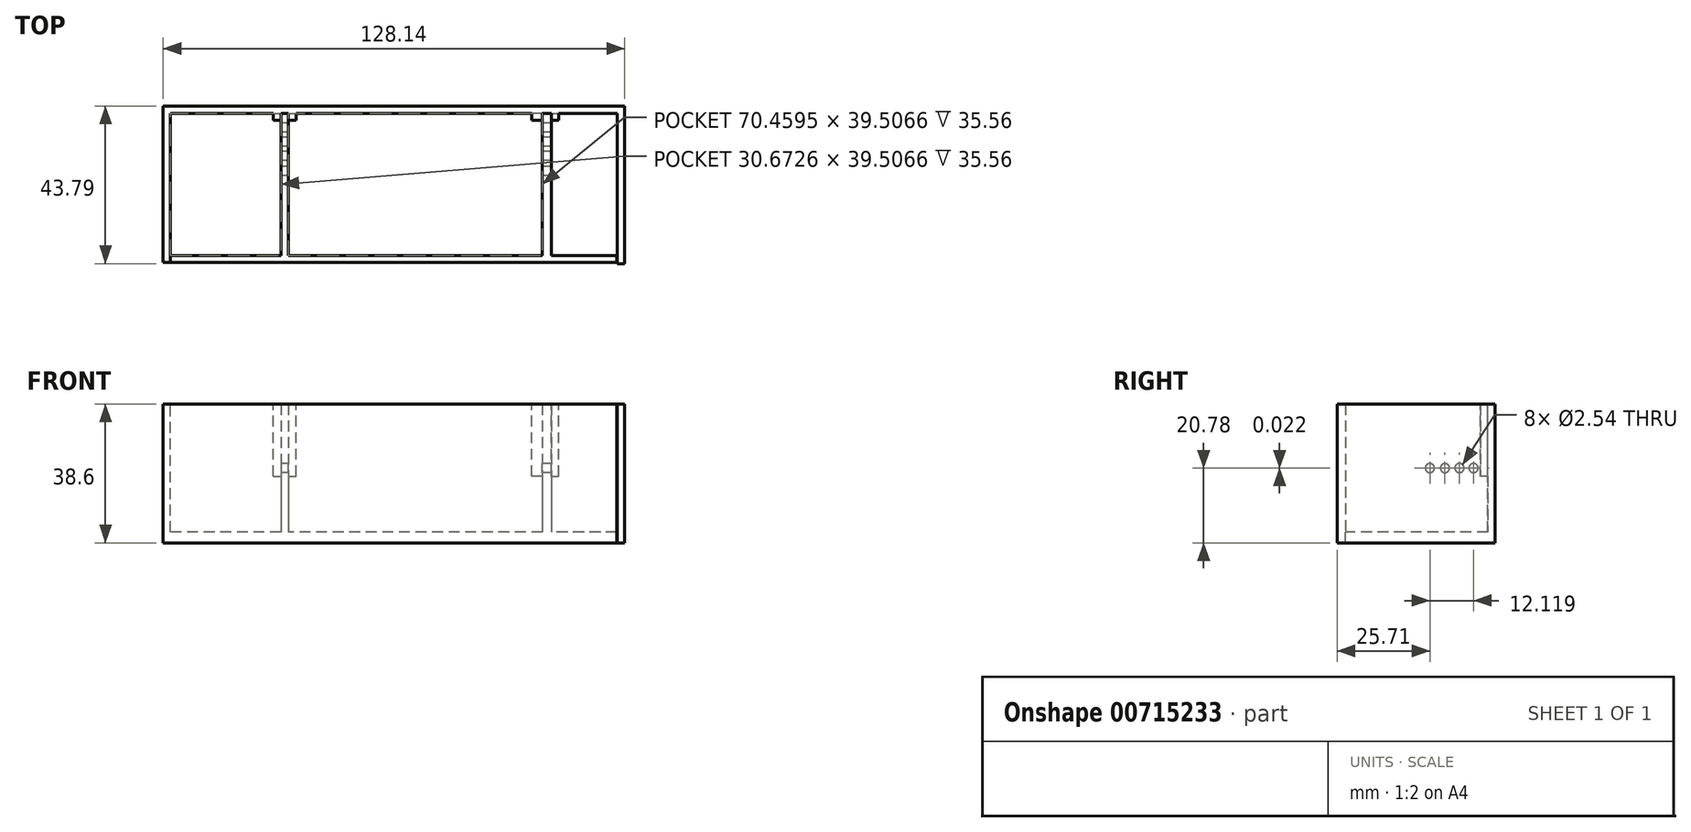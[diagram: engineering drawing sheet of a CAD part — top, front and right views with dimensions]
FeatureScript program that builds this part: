
annotation { "Feature Type Name" : "Feature", "Feature Type Description" : "" }
export const myFeature = defineFeature(function(context is Context, id is Id, definition is map)
    precondition{}
    {
        {
            var Q0;
            Q0=qCreatedBy(makeId("Top.planeOp"),FACE);
            var sketch = newSketch(context, id + "F0", { "sketchPlane" : qUnion([Q0])});
            skLineSegment(sketch, "E0.bottom", {"start": v(62.07, 19.75) * mm, "end": v(-62.07, 19.75) * mm});
            skLineSegment(sketch, "E0.top", {"start": v(62.07, -19.75) * mm, "end": v(-62.07, -19.75) * mm});
            skLineSegment(sketch, "E0.left", {"start": v(62.07, 19.75) * mm, "end": v(62.07, -19.75) * mm});
            skLineSegment(sketch, "E0.right", {"start": v(-62.07, 19.75) * mm, "end": v(-62.07, -19.75) * mm});
            skPoint(sketch, "E0.middle", {"position": v(0, 0) * mm});
            skSolve(sketch);
        }
        {
            var Q0;
            Q0=makeQuery(id+"F0.imprint","IMPRINT",FACE,{"disambiguationData":[TD([[makeQuery(id+"F0.imprint","IMPRINT",EDGE,{"derivedFrom":sQuery(id+"F0.wireOp",EDGE,"E0.bottom")}),1.0]])]});
            extrude(context, id + "F1", {"entities" : qUnion([Q0]), "depth" : 3 * mm, "offsetDistance" : 25.4 * mm});
        }
        {
            var Q0;
            Q0=makeQuery(id+"F1.opExtrude","CAP_FACE",FACE,{"disambiguationData":[OSD([sQuery(id+"F0.wireOp",EDGE,"E0.bottom"),sQuery(id+"F0.wireOp",EDGE,"E0.top"),sQuery(id+"F0.wireOp",EDGE,"E0.left"),sQuery(id+"F0.wireOp",EDGE,"E0.right")])],"isStart":false});
            var sketch = newSketch(context, id + "F2", { "sketchPlane" : qUnion([Q0])});
            skLineSegment(sketch, "E1.bottom", {"start": v(43.71, 19.75) * mm, "end": v(41.21, 19.75) * mm});
            skLineSegment(sketch, "E1.top", {"start": v(43.71, -19.75) * mm, "end": v(41.21, -19.75) * mm});
            skLineSegment(sketch, "E1.left", {"start": v(43.71, 19.75) * mm, "end": v(43.71, -19.75) * mm});
            skLineSegment(sketch, "E1.right", {"start": v(41.21, 19.75) * mm, "end": v(41.21, -19.75) * mm});
            skLineSegment(sketch, "E2.bottom", {"start": v(-29.25, 19.75) * mm, "end": v(-31.4, 19.75) * mm});
            skLineSegment(sketch, "E2.top", {"start": v(-29.25, -19.75) * mm, "end": v(-31.4, -19.75) * mm});
            skLineSegment(sketch, "E2.left", {"start": v(-29.25, 19.75) * mm, "end": v(-29.25, -19.75) * mm});
            skLineSegment(sketch, "E2.right", {"start": v(-31.4, 19.75) * mm, "end": v(-31.4, -19.75) * mm});
            skSolve(sketch);
        }
        {
            var Q0;
            Q0=makeQuery(id+"F2.imprint","IMPRINT",FACE,{"disambiguationData":[TD([[makeQuery(id+"F2.imprint","IMPRINT",EDGE,{"derivedFrom":sQuery(id+"F2.wireOp",EDGE,"E1.bottom")}),1.0]])]});
            var Q1;
            Q1=makeQuery(id+"F2.imprint","IMPRINT",FACE,{"disambiguationData":[TD([[makeQuery(id+"F2.imprint","IMPRINT",EDGE,{"derivedFrom":sQuery(id+"F2.wireOp",EDGE,"E2.bottom")}),1.0]])]});
            extrude(context, id + "F3", {"entities" : qUnion([Q0, Q1]), "operationType" : NewBodyOperationType.ADD, "depth" : 17.78 * mm, "offsetDistance" : 25.4 * mm});
        }
        {
            var Q0;
            Q0=makeQuery(id+"F3.opExtrude","SWEPT_FACE",FACE,{"disambiguationData":[OSD([sQuery(id+"F2.wireOp",EDGE,"E2.right")])]});
            var sketch = newSketch(context, id + "F4", { "sketchPlane" : qUnion([Q0])});
            skSolve(sketch);
        }
        {
            var Q0;
            Q0=makeQuery(id+"F3.opExtrude","CAP_FACE",FACE,{"disambiguationData":[OSD([sQuery(id+"F2.wireOp",EDGE,"E2.bottom"),sQuery(id+"F2.wireOp",EDGE,"E2.top"),sQuery(id+"F2.wireOp",EDGE,"E2.left"),sQuery(id+"F2.wireOp",EDGE,"E2.right")])],"isStart":false});
            var Q1;
            Q1=makeQuery(id+"F3.opExtrude","CAP_FACE",FACE,{"disambiguationData":[OSD([sQuery(id+"F2.wireOp",EDGE,"E1.bottom"),sQuery(id+"F2.wireOp",EDGE,"E1.top"),sQuery(id+"F2.wireOp",EDGE,"E1.left"),sQuery(id+"F2.wireOp",EDGE,"E1.right")])],"isStart":false});
            extrude(context, id + "F5", {"entities" : qUnion([Q0, Q1]), "operationType" : NewBodyOperationType.ADD, "depth" : 17.78 * mm, "offsetDistance" : 25.4 * mm});
        }
        {
            var Q0;
            {var subQ0=sQuery(id+"F2.wireOp",EDGE,"E2.right");Q0=makeQuery(id+"F5.boolean.opBoolean","MERGE",FACE,{"derivedFrom":[makeQuery(id+"F3.opExtrude","SWEPT_FACE",FACE,{"disambiguationData":[OSD([subQ0])]}),makeQuery(id+"F5.opExtrude","SWEPT_FACE",FACE,{"disambiguationData":[OSD([subQ0])]})]});}
            var sketch = newSketch(context, id + "F6", { "sketchPlane" : qUnion([Q0])});
            skCircle(sketch, "E3", {"center": v(-15.79, 20.8) * mm, "radius": 1.27 * mm});
            skCircle(sketch, "E4", {"center": v(-11.89, 20.8) * mm, "radius": 1.27 * mm});
            skCircle(sketch, "E5", {"center": v(-7.85, 20.78) * mm, "radius": 1.27 * mm});
            skCircle(sketch, "E6", {"center": v(-3.67, 20.79) * mm, "radius": 1.27 * mm});
            skSolve(sketch);
        }
        {
            var Q0;
            Q0=sQuery(id+"F6.wireOp",VERTEX,"E4.center");
            var Q1;
            Q1=sQuery(id+"F6.wireOp",VERTEX,"E3.center");
            var Q2;
            Q2=sQuery(id+"F6.wireOp",VERTEX,"E5.center");
            var Q3;
            Q3=sQuery(id+"F6.wireOp",VERTEX,"E6.center");
            var Q4;
            Q4=makeQuery(id+"F1.opExtrude","SWEPT_BODY",BODY,{"disambiguationData":[OSD([sQuery(id+"F0.wireOp",EDGE,"E0.bottom"),sQuery(id+"F0.wireOp",EDGE,"E0.top"),sQuery(id+"F0.wireOp",EDGE,"E0.left"),sQuery(id+"F0.wireOp",EDGE,"E0.right")])]});
            hole(context, id + "F7", {"style" : HoleStyle.SIMPLE, "endStyle" : HoleEndStyle.THROUGH, "holeDiameter" : 2.54 * mm, "majorDiameter" : 6.35 * mm, "isTappedThrough" : true, "tappedDepth" : 12.7 * mm, "tapClearance" : 3, "locations" : qUnion([Q0, Q1, Q2, Q3]), "scope" : qUnion([Q4])});
        }
        {
            var Q0;
            {var subQ0=sQuery(id+"F2.wireOp",EDGE,"E2.top");var subQ1=sQuery(id+"F2.wireOp",EDGE,"E1.top");Q0=makeQuery(id+"F5.boolean.opBoolean","MERGE",FACE,{"derivedFrom":[makeQuery(id+"F3.boolean.opBoolean","MERGE",FACE,{"derivedFrom":[makeQuery(id+"F1.opExtrude","SWEPT_FACE",FACE,{"disambiguationData":[OSD([sQuery(id+"F0.wireOp",EDGE,"E0.top")])]}),makeQuery(id+"F3.opExtrude","SWEPT_FACE",FACE,{"disambiguationData":[OSD([subQ1])]}),makeQuery(id+"F3.opExtrude","SWEPT_FACE",FACE,{"disambiguationData":[OSD([subQ0])]})]}),makeQuery(id+"F5.opExtrude","SWEPT_FACE",FACE,{"disambiguationData":[OSD([subQ1])]}),makeQuery(id+"F5.opExtrude","SWEPT_FACE",FACE,{"disambiguationData":[OSD([subQ0])]})]});}
            var sketch = newSketch(context, id + "F8", { "sketchPlane" : qUnion([Q0])});
            skLineSegment(sketch, "E7.bottom", {"start": v(-62.07, 0) * mm, "end": v(61.89, 0) * mm});
            skLineSegment(sketch, "E7.top", {"start": v(-62.07, 38.56) * mm, "end": v(61.89, 38.56) * mm});
            skLineSegment(sketch, "E7.left", {"start": v(-62.07, 0) * mm, "end": v(-62.07, 38.56) * mm});
            skLineSegment(sketch, "E7.right", {"start": v(61.89, 0) * mm, "end": v(61.89, 38.56) * mm});
            skSolve(sketch);
        }
        {
            var Q0;
            {var subQ1=sQuery(id+"F2.wireOp",EDGE,"E2.right");var subQ2=sQuery(id+"F2.wireOp",EDGE,"E2.top");var subQ3=sQuery(id+"F0.wireOp",EDGE,"E0.top");var subQ4=makeQuery(id+"F5.boolean.opBoolean","MERGE",EDGE,{"derivedFrom":[makeQuery(id+"F3.opExtrude","SWEPT_EDGE",EDGE,{"disambiguationData":[OSD([subQ3,subQ2,subQ1])]}),makeQuery(id+"F5.opExtrude","SWEPT_EDGE",EDGE,{"disambiguationData":[OSD([subQ3,subQ2,subQ1])]})]});Q0=makeQuery(id+"F8.imprint","IMPRINT",FACE,{"disambiguationData":[TD([[makeQuery(id+"F8.imprint","IMPRINT",EDGE,{"derivedFrom":subQ4}),-1.0]])]});}
            var Q1;
            {var subQ1=sQuery(id+"F2.wireOp",EDGE,"E1.right");var subQ2=sQuery(id+"F2.wireOp",EDGE,"E1.top");var subQ3=sQuery(id+"F0.wireOp",EDGE,"E0.top");var subQ4=makeQuery(id+"F5.boolean.opBoolean","MERGE",EDGE,{"derivedFrom":[makeQuery(id+"F3.opExtrude","SWEPT_EDGE",EDGE,{"disambiguationData":[OSD([subQ3,subQ2,subQ1])]}),makeQuery(id+"F5.opExtrude","SWEPT_EDGE",EDGE,{"disambiguationData":[OSD([subQ3,subQ2,subQ1])]})]});Q1=makeQuery(id+"F8.imprint","IMPRINT",FACE,{"disambiguationData":[TD([[makeQuery(id+"F8.imprint","IMPRINT",EDGE,{"derivedFrom":subQ4}),-1.0]])]});}
            var Q2;
            {var subQ1=sQuery(id+"F2.wireOp",EDGE,"E1.left");var subQ2=sQuery(id+"F2.wireOp",EDGE,"E1.top");var subQ3=sQuery(id+"F0.wireOp",EDGE,"E0.top");var subQ4=makeQuery(id+"F5.boolean.opBoolean","MERGE",EDGE,{"derivedFrom":[makeQuery(id+"F3.opExtrude","SWEPT_EDGE",EDGE,{"disambiguationData":[OSD([subQ3,subQ2,subQ1])]}),makeQuery(id+"F5.opExtrude","SWEPT_EDGE",EDGE,{"disambiguationData":[OSD([subQ3,subQ2,subQ1])]})]});Q2=makeQuery(id+"F8.imprint","IMPRINT",FACE,{"disambiguationData":[TD([[makeQuery(id+"F8.imprint","IMPRINT",EDGE,{"derivedFrom":subQ4}),1.0]])]});}
            var Q3;
            {var subQ17=sQuery(id+"F8.wireOp",EDGE,"E7.bottom");Q3=makeQuery(id+"F8.imprint","IMPRINT",FACE,{"disambiguationData":[TD([[makeQuery(id+"F8.imprint","IMPRINT",EDGE,{"derivedFrom":subQ17}),-1.0]])]});}
            extrude(context, id + "F9", {"entities" : qUnion([Q0, Q1, Q2, Q3]), "operationType" : NewBodyOperationType.ADD, "depth" : 2 * mm, "offsetDistance" : 25.4 * mm});
        }
        {
            var Q0;
            {var subQ0=sQuery(id+"F2.wireOp",EDGE,"E2.bottom");var subQ1=sQuery(id+"F2.wireOp",EDGE,"E1.bottom");Q0=makeQuery(id+"F5.boolean.opBoolean","MERGE",FACE,{"derivedFrom":[makeQuery(id+"F3.boolean.opBoolean","MERGE",FACE,{"derivedFrom":[makeQuery(id+"F1.opExtrude","SWEPT_FACE",FACE,{"disambiguationData":[OSD([sQuery(id+"F0.wireOp",EDGE,"E0.bottom")])]}),makeQuery(id+"F3.opExtrude","SWEPT_FACE",FACE,{"disambiguationData":[OSD([subQ1])]}),makeQuery(id+"F3.opExtrude","SWEPT_FACE",FACE,{"disambiguationData":[OSD([subQ0])]})]}),makeQuery(id+"F5.opExtrude","SWEPT_FACE",FACE,{"disambiguationData":[OSD([subQ1])]}),makeQuery(id+"F5.opExtrude","SWEPT_FACE",FACE,{"disambiguationData":[OSD([subQ0])]})]});}
            var sketch = newSketch(context, id + "F10", { "sketchPlane" : qUnion([Q0])});
            skLineSegment(sketch, "E8.bottom", {"start": v(-62.07, 0) * mm, "end": v(62.07, 0) * mm});
            skLineSegment(sketch, "E8.top", {"start": v(-62.07, 38.6) * mm, "end": v(62.07, 38.6) * mm});
            skLineSegment(sketch, "E8.left", {"start": v(-62.07, 0) * mm, "end": v(-62.07, 38.6) * mm});
            skLineSegment(sketch, "E8.right", {"start": v(62.07, 0) * mm, "end": v(62.07, 38.6) * mm});
            skSolve(sketch);
        }
        {
            var Q0;
            {var subQ15=sQuery(id+"F10.wireOp",EDGE,"E8.top");Q0=makeQuery(id+"F10.imprint","IMPRINT",FACE,{"disambiguationData":[TD([[makeQuery(id+"F10.imprint","IMPRINT",EDGE,{"derivedFrom":subQ15}),-1.0]])]});}
            var Q1;
            {var subQ15=sQuery(id+"F10.wireOp",EDGE,"E8.bottom");Q1=makeQuery(id+"F10.imprint","IMPRINT",FACE,{"disambiguationData":[TD([[makeQuery(id+"F10.imprint","IMPRINT",EDGE,{"derivedFrom":subQ15}),1.0]])]});}
            extrude(context, id + "F11", {"entities" : qUnion([Q0, Q1]), "operationType" : NewBodyOperationType.ADD, "depth" : 2 * mm, "offsetDistance" : 25.4 * mm});
        }
        {
            var Q0;
            Q0=makeQuery(id+"F11.boolean.opBoolean","MERGE",FACE,{"derivedFrom":[makeQuery(id+"F1.opExtrude","SWEPT_FACE",FACE,{"disambiguationData":[OSD([sQuery(id+"F0.wireOp",EDGE,"E0.left")])]}),makeQuery(id+"F11.opExtrude","SWEPT_FACE",FACE,{"disambiguationData":[OSD([sQuery(id+"F10.wireOp",EDGE,"E8.left")])]})]});
            var sketch = newSketch(context, id + "F12", { "sketchPlane" : qUnion([Q0])});
            skLineSegment(sketch, "E9.bottom", {"start": v(21.75, 38.6) * mm, "end": v(-22.04, 38.6) * mm});
            skLineSegment(sketch, "E9.top", {"start": v(21.75, 0) * mm, "end": v(-22.04, 0) * mm});
            skLineSegment(sketch, "E9.left", {"start": v(21.75, 38.6) * mm, "end": v(21.75, 0) * mm});
            skLineSegment(sketch, "E9.right", {"start": v(-22.04, 38.6) * mm, "end": v(-22.04, 0) * mm});
            skSolve(sketch);
        }
        {
            var Q0;
            {var subQ3=sQuery(id+"F12.wireOp",EDGE,"E9.right");Q0=makeQuery(id+"F12.imprint","IMPRINT",FACE,{"disambiguationData":[TD([[makeQuery(id+"F12.imprint","IMPRINT",EDGE,{"derivedFrom":subQ3}),1.0]])]});}
            var Q1;
            {var subQ0=sQuery(id+"F12.wireOp",EDGE,"E9.left");Q1=makeQuery(id+"F12.imprint","IMPRINT",FACE,{"disambiguationData":[TD([[makeQuery(id+"F12.imprint","IMPRINT",EDGE,{"derivedFrom":subQ0}),1.0]])]});}
            extrude(context, id + "F13", {"entities" : qUnion([Q0, Q1]), "operationType" : NewBodyOperationType.ADD, "depth" : 2 * mm, "offsetDistance" : 25.4 * mm});
        }
        {
            var Q0;
            Q0=makeQuery(id+"F11.boolean.opBoolean","MERGE",FACE,{"derivedFrom":[makeQuery(id+"F9.boolean.opBoolean","MERGE",FACE,{"derivedFrom":[makeQuery(id+"F1.opExtrude","SWEPT_FACE",FACE,{"disambiguationData":[OSD([sQuery(id+"F0.wireOp",EDGE,"E0.right")])]}),makeQuery(id+"F9.opExtrude","SWEPT_FACE",FACE,{"disambiguationData":[OSD([sQuery(id+"F8.wireOp",EDGE,"E7.left")])]})]}),makeQuery(id+"F11.opExtrude","SWEPT_FACE",FACE,{"disambiguationData":[OSD([sQuery(id+"F10.wireOp",EDGE,"E8.right")])]})]});
            var sketch = newSketch(context, id + "F14", { "sketchPlane" : qUnion([Q0])});
            skLineSegment(sketch, "E10.bottom", {"start": v(21.75, 0) * mm, "end": v(-21.75, 0) * mm});
            skLineSegment(sketch, "E10.top", {"start": v(21.75, 38.6) * mm, "end": v(-21.75, 38.6) * mm});
            skLineSegment(sketch, "E10.left", {"start": v(21.75, 0) * mm, "end": v(21.75, 38.6) * mm});
            skLineSegment(sketch, "E10.right", {"start": v(-21.75, 0) * mm, "end": v(-21.75, 38.6) * mm});
            skSolve(sketch);
        }
        {
            var Q0;
            {var subQ1=sQuery(id+"F14.wireOp",EDGE,"E10.bottom");Q0=makeQuery(id+"F14.imprint","IMPRINT",FACE,{"disambiguationData":[TD([[makeQuery(id+"F14.imprint","IMPRINT",EDGE,{"derivedFrom":subQ1}),1.0]])]});}
            var Q1;
            Q1=makeQuery(id+"F14.imprint","IMPRINT",FACE,{"disambiguationData":[TD([[makeQuery(id+"F14.imprint","IMPRINT",EDGE,{"derivedFrom":makeQuery(id+"F1.opExtrude","CAP_EDGE",EDGE,{"disambiguationData":[OSD([sQuery(id+"F0.wireOp",EDGE,"E0.right")])],"isStart":false})}),1.0]])]});
            extrude(context, id + "F15", {"entities" : qUnion([Q0, Q1]), "operationType" : NewBodyOperationType.ADD, "depth" : 2 * mm, "offsetDistance" : 25.4 * mm});
        }
        {
            var Q0;
            Q0=makeQuery(id+"F11.opExtrude","CAP_FACE",FACE,{"disambiguationData":[OSD([sQuery(id+"F10.wireOp",EDGE,"E8.bottom"),sQuery(id+"F10.wireOp",EDGE,"E8.top"),sQuery(id+"F10.wireOp",EDGE,"E8.left"),sQuery(id+"F10.wireOp",EDGE,"E8.right")])],"isStart":true});
            var sketch = newSketch(context, id + "F16", { "sketchPlane" : qUnion([Q0])});
            skLineSegment(sketch, "E11.bottom", {"start": v(41.21, 18.56) * mm, "end": v(38.26, 18.56) * mm});
            skLineSegment(sketch, "E11.top", {"start": v(41.21, 38.6) * mm, "end": v(38.26, 38.6) * mm});
            skLineSegment(sketch, "E11.left", {"start": v(41.21, 18.56) * mm, "end": v(41.21, 38.6) * mm});
            skLineSegment(sketch, "E11.right", {"start": v(38.26, 18.56) * mm, "end": v(38.26, 38.6) * mm});
            skLineSegment(sketch, "E12.bottom", {"start": v(-31.4, 18.56) * mm, "end": v(-29.25, 18.56) * mm});
            skLineSegment(sketch, "E12.top", {"start": v(-31.4, 38.56) * mm, "end": v(-29.25, 38.56) * mm});
            skLineSegment(sketch, "E12.left", {"start": v(-31.4, 18.56) * mm, "end": v(-31.4, 38.56) * mm});
            skLineSegment(sketch, "E12.right", {"start": v(-29.25, 18.56) * mm, "end": v(-29.25, 38.56) * mm});
            skLineSegment(sketch, "E13.bottom", {"start": v(-29.25, 18.56) * mm, "end": v(-27.1, 18.56) * mm});
            skLineSegment(sketch, "E13.top", {"start": v(-29.25, 38.6) * mm, "end": v(-27.1, 38.6) * mm});
            skLineSegment(sketch, "E13.left", {"start": v(-29.25, 18.56) * mm, "end": v(-29.25, 38.6) * mm});
            skLineSegment(sketch, "E13.right", {"start": v(-27.1, 18.56) * mm, "end": v(-27.1, 38.6) * mm});
            skLineSegment(sketch, "E14.bottom", {"start": v(-31.4, 18.56) * mm, "end": v(-33.44, 18.56) * mm});
            skLineSegment(sketch, "E14.top", {"start": v(-31.4, 38.6) * mm, "end": v(-33.44, 38.6) * mm});
            skLineSegment(sketch, "E14.left", {"start": v(-31.4, 18.56) * mm, "end": v(-31.4, 38.6) * mm});
            skLineSegment(sketch, "E14.right", {"start": v(-33.44, 18.56) * mm, "end": v(-33.44, 38.6) * mm});
            skLineSegment(sketch, "E15.bottom", {"start": v(43.71, 18.56) * mm, "end": v(45.76, 18.56) * mm});
            skLineSegment(sketch, "E15.top", {"start": v(43.71, 38.6) * mm, "end": v(45.76, 38.6) * mm});
            skLineSegment(sketch, "E15.left", {"start": v(43.71, 18.56) * mm, "end": v(43.71, 38.6) * mm});
            skLineSegment(sketch, "E15.right", {"start": v(45.76, 18.56) * mm, "end": v(45.76, 38.6) * mm});
            skSolve(sketch);
        }
        {
            var Q0;
            Q0 = qSketchRegion(id + "F16", true);
            extrude(context, id + "F17", {"entities" : qUnion([Q0]), "operationType" : NewBodyOperationType.ADD, "depth" : 2 * mm, "offsetDistance" : 25.4 * mm});
        }
    });
